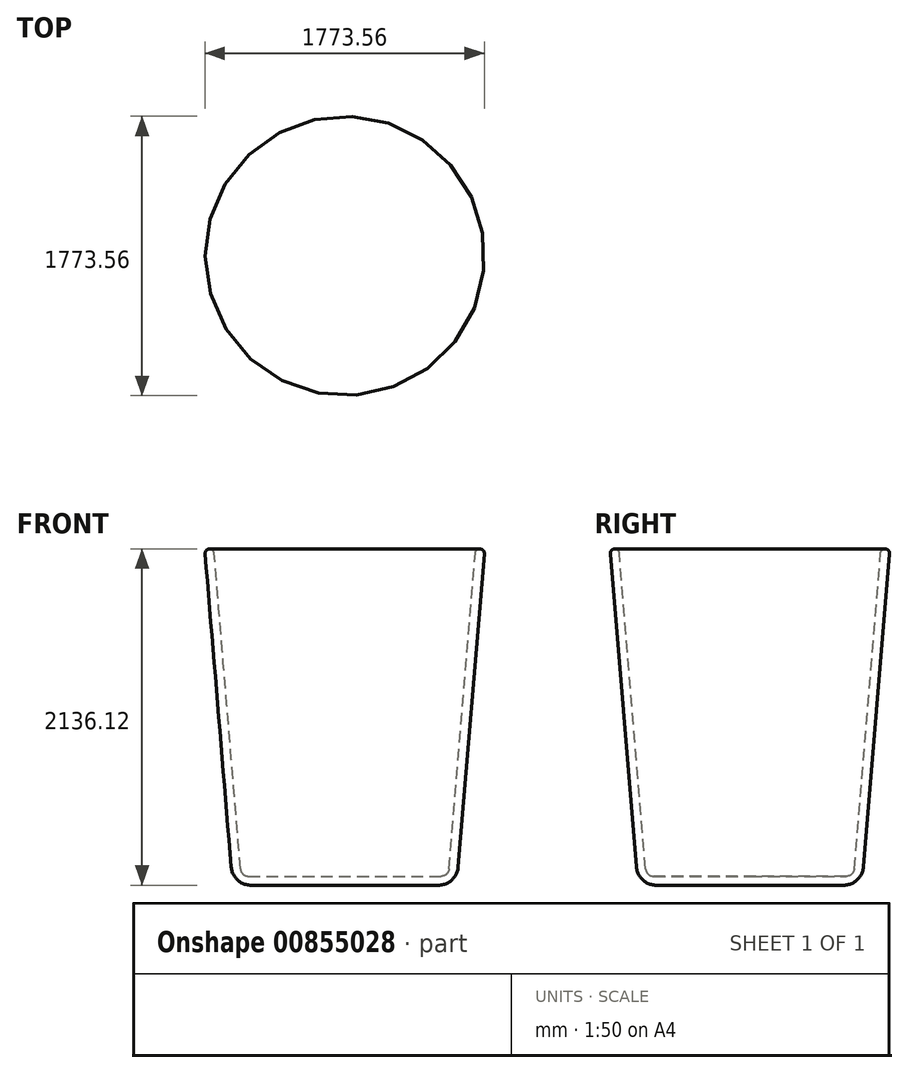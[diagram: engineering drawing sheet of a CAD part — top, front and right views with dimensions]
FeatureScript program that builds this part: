
annotation { "Feature Type Name" : "Feature", "Feature Type Description" : "" }
export const myFeature = defineFeature(function(context is Context, id is Id, definition is map)
    precondition{}
    {
        {
            var Q0;
            Q0=qCreatedBy(makeId("Front.planeOp"),FACE);
            var sketch = newSketch(context, id + "F0", { "sketchPlane" : qUnion([Q0])});
            skLineSegment(sketch, "E0", {"start": v(116.86, 0) * mm, "end": v(711.2, 0) * mm});
            skLineSegment(sketch, "E1", {"start": v(-9.7, 116.45) * mm, "end": v(-175.48, 2105.76) * mm});
            skLineSegment(sketch, "E2", {"start": v(711.2, 0) * mm, "end": v(711.2, 2133.6) * mm});
            skLineSegment(sketch, "E3.0", {"start": v(48.7, 103.73) * mm, "end": v(-118.53, 2110.5) * mm});
            skLineSegment(sketch, "E3.1", {"start": v(99.33, 57.15) * mm, "end": v(711.2, 57.15) * mm});
            skPoint(sketch, "E4.visualSharp", {"position": v(52.59, 57.15) * mm});
            skArc(sketch, "E4.filletArc", {"start": v(48.7, 103.73) * mm, "mid": v(64.93, 70.57) * mm, "end": v(99.33, 57.15) * mm});
            skPoint(sketch, "E5.visualSharp", {"position": v(0, 0) * mm});
            skArc(sketch, "E5.filletArc", {"start": v(-9.7, 116.45) * mm, "mid": v(30.86, 33.54) * mm, "end": v(116.86, 0) * mm});
            skLineSegment(sketch, "E6", {"start": v(-149.96, 2135.92) * mm, "end": v(-148.7, 2136.03) * mm});
            skPoint(sketch, "E7.visualSharp", {"position": v(-177.8, 2133.6) * mm});
            skArc(sketch, "E7.filletArc", {"start": v(-149.96, 2135.92) * mm, "mid": v(-168.97, 2126.12) * mm, "end": v(-175.48, 2105.76) * mm});
            skPoint(sketch, "E8.visualSharp", {"position": v(-120.85, 2138.35) * mm});
            skArc(sketch, "E8.filletArc", {"start": v(-118.53, 2110.5) * mm, "mid": v(-128.32, 2129.51) * mm, "end": v(-148.7, 2136.03) * mm});
            skSolve(sketch);
        }
        {
            var Q0;
            Q0 = qSketchRegion(id + "F0", true);
            var Q1;
            Q1=sQuery(id+"F0.wireOp",EDGE,"E2");
            revolve(context, id + "F1", {"surfaceOperationType" : NewSurfaceOperationType.NEW, "entities" : qUnion([Q0]), "axis" : qUnion([Q1]), "revolveType" : RevolveType.FULL});
        }
    });
